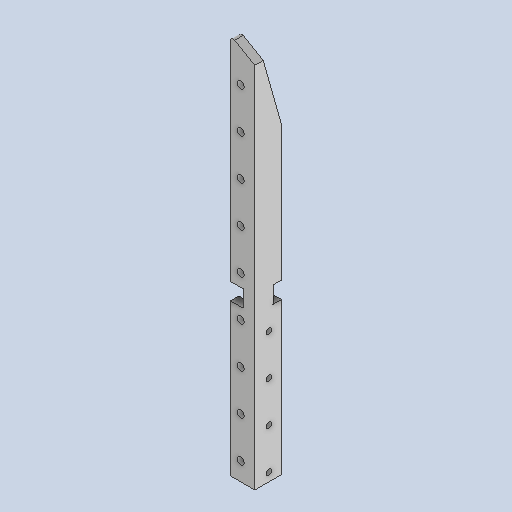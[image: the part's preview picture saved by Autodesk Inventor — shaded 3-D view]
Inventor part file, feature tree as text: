
AUTODESK INVENTOR PART (.ipt)
format: ipt  version: 2025.1 (Build 291241000, 241)  size: 138,752 bytes
history: native  units: mm
features: sketch x6, other x3
ambient origin geometry x8: Origin, YZ Plane, XZ Plane, XY Plane, X Axis, Y Axis, Z Axis, Center Point
bodies: Solid1 (feature_tree)
feature tree (9):
  other  "1013.ipt"
  other  "Solid1::1013.ipt"
  other  "TaggingFeature1"
  sketch  "Sketch1"  dims[d0=10.0mm]
  sketch  "Sketch2"
  sketch  "Sketch3"
  sketch  "Sketch4"
  sketch  "Sketch5"
  sketch  "Sketch6"
